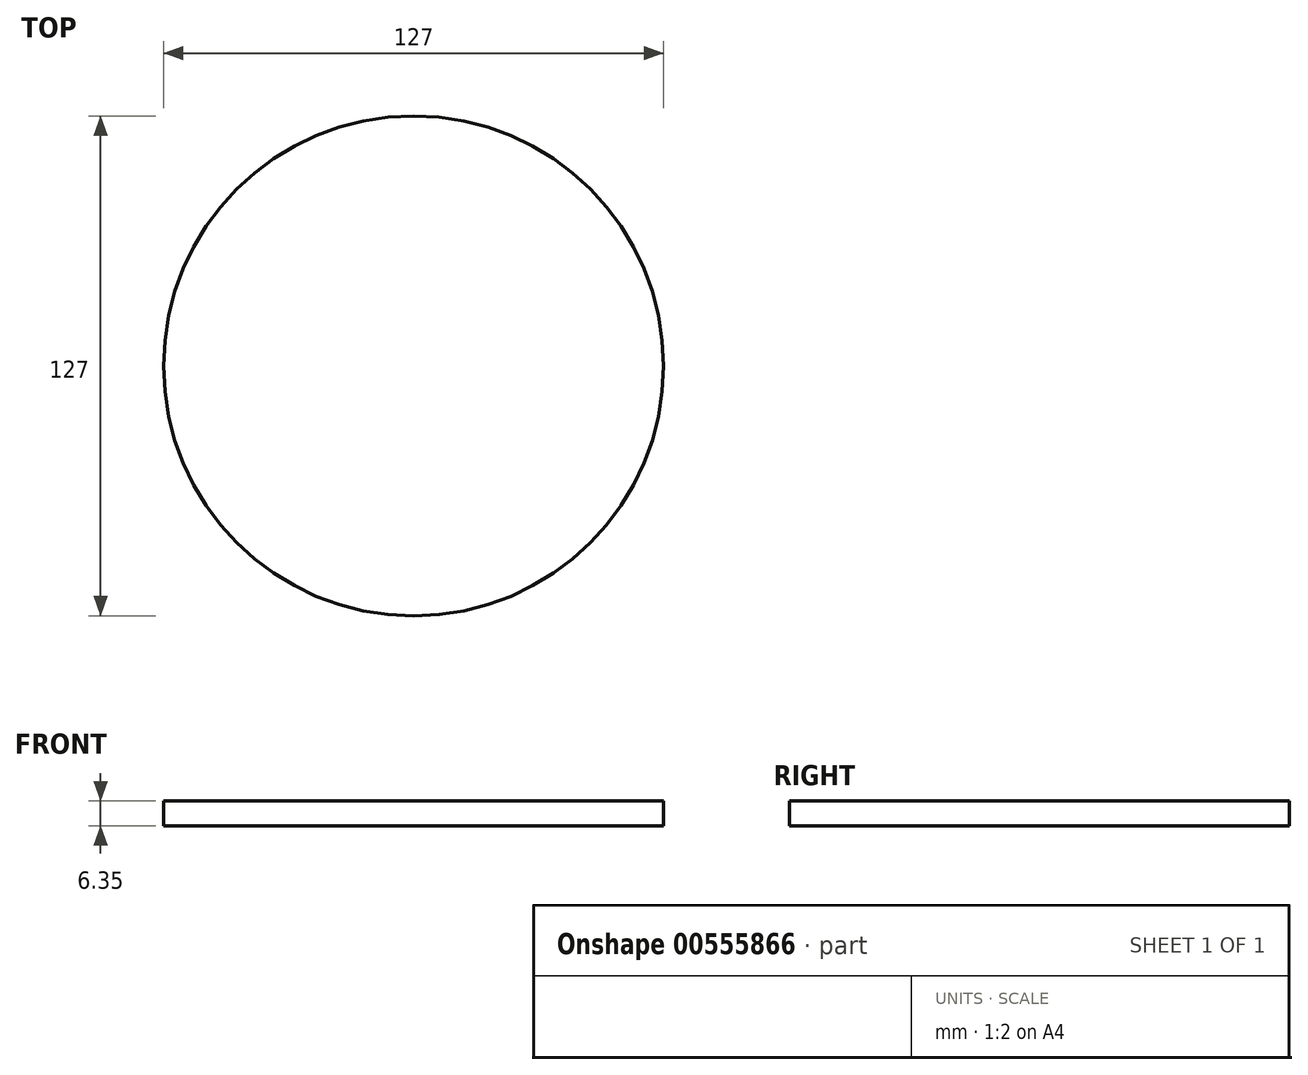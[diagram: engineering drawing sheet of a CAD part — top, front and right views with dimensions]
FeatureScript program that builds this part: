
annotation { "Feature Type Name" : "Feature", "Feature Type Description" : "" }
export const myFeature = defineFeature(function(context is Context, id is Id, definition is map)
    precondition{}
    {
        {
            var Q0;
            Q0=qCreatedBy(makeId("Top.planeOp"),FACE);
            var sketch = newSketch(context, id + "F0", { "sketchPlane" : qUnion([Q0])});
            skCircle(sketch, "E0", {"center": v(0, 0) * mm, "radius": 63.5 * mm});
            skSolve(sketch);
        }
        {
            var Q0;
            Q0 = qSketchRegion(id + "F0", true);
            extrude(context, id + "F1", {"entities" : qUnion([Q0]), "depth" : 6.35 * mm, "offsetDistance" : 25.4 * mm});
        }
    });
